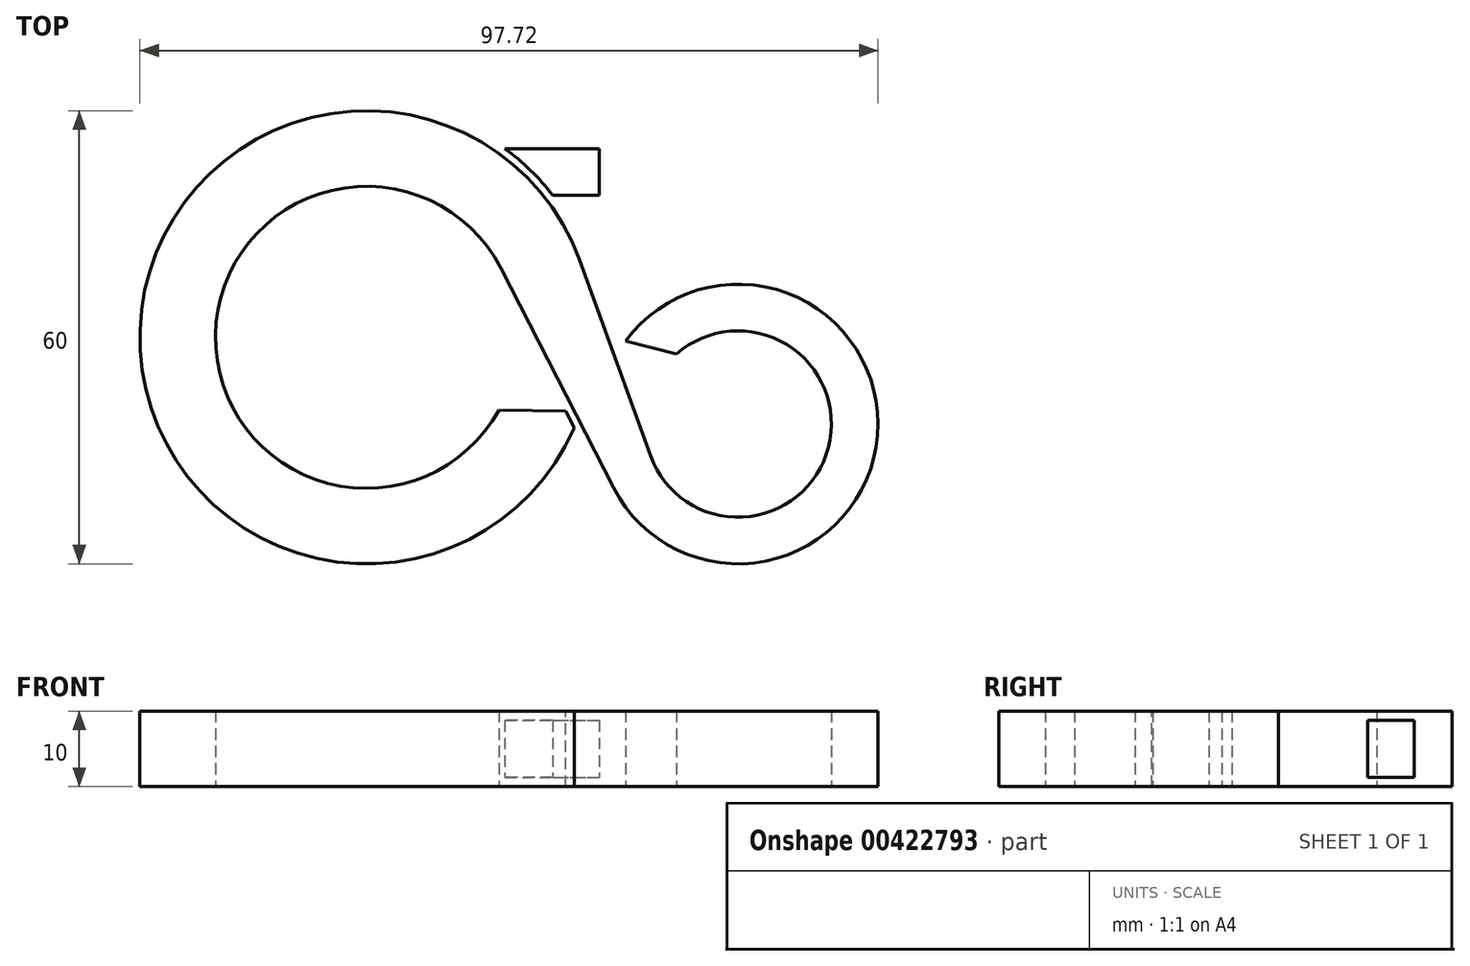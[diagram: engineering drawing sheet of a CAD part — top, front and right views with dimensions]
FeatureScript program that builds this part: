
annotation { "Feature Type Name" : "Feature", "Feature Type Description" : "" }
export const myFeature = defineFeature(function(context is Context, id is Id, definition is map)
    precondition{}
    {
        {
            var Q0;
            Q0=qCreatedBy(makeId("Top.planeOp"),FACE);
            var sketch = newSketch(context, id + "F0", { "sketchPlane" : qUnion([Q0])});
            skCircle(sketch, "E0", {"center": v(0, 0) * mm, "radius": 30 * mm});
            skCircle(sketch, "E1", {"center": v(0, 0) * mm, "radius": 20 * mm});
            skCircle(sketch, "E2", {"center": v(49.2, -11.48) * mm, "radius": 18.52 * mm});
            skCircle(sketch, "E3", {"center": v(49.2, -11.48) * mm, "radius": 12.35 * mm});
            skLineSegment(sketch, "E4", {"start": v(0, -30) * mm, "end": v(49.2, -30) * mm, "construction": true});
            skLineSegment(sketch, "E5", {"start": v(17.8, 9.14) * mm, "end": v(32.72, -19.94) * mm});
            skLineSegment(sketch, "E6", {"start": v(28.2, 10.22) * mm, "end": v(37.59, -15.69) * mm});
            skLineSegment(sketch, "E7", {"start": v(19.75, 3.12) * mm, "end": v(27.5, -11.97) * mm});
            skLineSegment(sketch, "E8", {"start": v(33.54, -1.58) * mm, "end": v(36.87, -10.77) * mm});
            skLineSegment(sketch, "E9.right", {"start": v(30.8, 25) * mm, "end": v(30.8, 18.83) * mm});
            skArc(sketch, "E10", {"start": v(24.63, 18.83) * mm, "mid": v(21.7, 22.14) * mm, "end": v(18.33, 25) * mm});
            skLineSegment(sketch, "E11.trimOffspring", {"start": v(18.33, 25) * mm, "end": v(30.8, 25) * mm});
            skLineSegment(sketch, "E12.trimOffspring", {"start": v(24.63, 18.83) * mm, "end": v(30.8, 18.83) * mm});
            skSolve(sketch);
        }
        {
            var Q0;
            {var subQ3=sQuery(id+"F0.wireOp",EDGE,"E7");Q0=makeQuery(id+"F0.imprint","IMPRINT",FACE,{"disambiguationData":[TD([[makeQuery(id+"F0.imprint","IMPRINT",EDGE,{"derivedFrom":subQ3}),-1.0]])]});}
            var Q1;
            {var subQ0=sQuery(id+"F0.wireOp",EDGE,"E6");var subQ1=sQuery(id+"F0.wireOp",EDGE,"E0");var subQ2=makeQuery(id+"F0.imprint","INTERSECT",VERTEX,{"derivedFrom":[subQ1,subQ0]});Q1=makeQuery(id+"F0.imprint","IMPRINT",FACE,{"disambiguationData":[TD([[makeQuery(id+"F0.imprint","IMPRINT",EDGE,{"disambiguationData":[TD([[subQ2,1.0]])],"derivedFrom":subQ1}),-1.0]])]});}
            var Q2;
            {var subQ5=sQuery(id+"F0.wireOp",EDGE,"E8");Q2=makeQuery(id+"F0.imprint","IMPRINT",FACE,{"disambiguationData":[TD([[makeQuery(id+"F0.imprint","IMPRINT",EDGE,{"derivedFrom":subQ5}),1.0]])]});}
            extrude(context, id + "F1", {"entities" : qUnion([Q0, Q1, Q2]), "depth" : 10 * mm, "symmetric" : true});
        }
        {
            var Q0;
            Q0=makeQuery(id+"F1.opExtrude","SWEPT_EDGE",EDGE,{"disambiguationData":[OSD([sQuery(id+"F0.wireOp",EDGE,"E1"),sQuery(id+"F0.wireOp",EDGE,"E7")])]});
            var Q1;
            Q1=makeQuery(id+"F1.opExtrude","SWEPT_EDGE",EDGE,{"disambiguationData":[OSD([sQuery(id+"F0.wireOp",EDGE,"E3"),sQuery(id+"F0.wireOp",EDGE,"E8")])]});
            chamfer(context, id + "F2", {"entities" : qUnion([Q0, Q1]), "width" : 5 * mm, "tangentPropagation" : true});
        }
        {
            var Q0;
            Q0=makeQuery(id+"F0.imprint","IMPRINT",FACE,{"disambiguationData":[TD([[makeQuery(id+"F0.imprint","IMPRINT",EDGE,{"derivedFrom":sQuery(id+"F0.wireOp",EDGE,"E9.right")}),-1.0]])]});
            extrude(context, id + "F3", {"entities" : qUnion([Q0]), "operationType" : NewBodyOperationType.ADD, "depth" : 7.5 * mm, "symmetric" : true});
        }
    });
